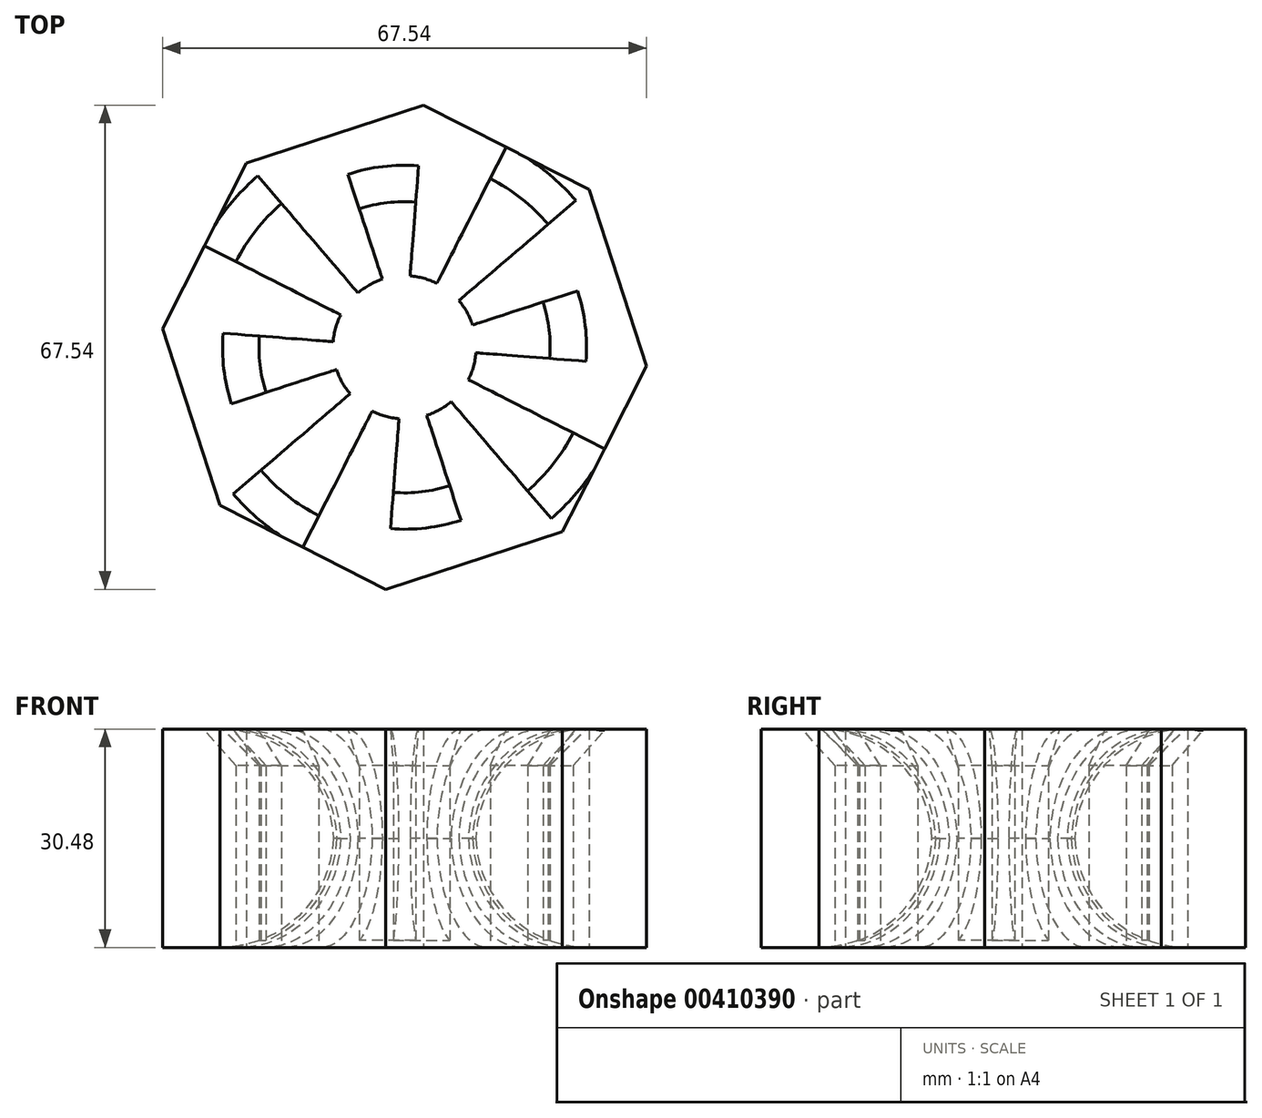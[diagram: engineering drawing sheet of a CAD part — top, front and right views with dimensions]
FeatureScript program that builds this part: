
annotation { "Feature Type Name" : "Feature", "Feature Type Description" : "" }
export const myFeature = defineFeature(function(context is Context, id is Id, definition is map)
    precondition{}
    {
        {
            var Q0;
            Q0=qCreatedBy(makeId("Top.planeOp"),FACE);
            var sketch = newSketch(context, id + "F0", { "sketchPlane" : qUnion([Q0])});
            skCircle(sketch, "E0.cCircle", {"center": v(0, 0) * mm, "radius": 31.3 * mm, "construction": true});
            skLineSegment(sketch, "E0.0", {"start": v(-33.77, 2.61) * mm, "end": v(-22.03, 25.73) * mm});
            skLineSegment(sketch, "E0.1", {"start": v(-22.03, 25.73) * mm, "end": v(2.61, 33.77) * mm});
            skLineSegment(sketch, "E0.2", {"start": v(2.61, 33.77) * mm, "end": v(25.73, 22.03) * mm});
            skLineSegment(sketch, "E0.3", {"start": v(25.73, 22.03) * mm, "end": v(33.77, -2.61) * mm});
            skLineSegment(sketch, "E0.4", {"start": v(33.77, -2.61) * mm, "end": v(22.03, -25.73) * mm});
            skLineSegment(sketch, "E0.5", {"start": v(22.03, -25.73) * mm, "end": v(-2.61, -33.77) * mm});
            skLineSegment(sketch, "E0.6", {"start": v(-2.61, -33.77) * mm, "end": v(-25.73, -22.03) * mm});
            skLineSegment(sketch, "E0.7", {"start": v(-25.73, -22.03) * mm, "end": v(-33.77, 2.61) * mm});
            skPoint(sketch, "E0.0.midPoint", {"position": v(-27.9, 14.17) * mm});
            skLineSegment(sketch, "E1", {"start": v(-0.77, -9.95) * mm, "end": v(-2.61, -33.77) * mm});
            skLineSegment(sketch, "E2", {"start": v(9.71, -29.75) * mm, "end": v(3.1, -9.49) * mm});
            skLineSegment(sketch, "E3", {"start": v(22.03, -25.73) * mm, "end": v(6.5, -7.58) * mm});
            skLineSegment(sketch, "E4", {"start": v(27.9, -14.17) * mm, "end": v(8.9, -4.52) * mm});
            skLineSegment(sketch, "E5", {"start": v(33.77, -2.61) * mm, "end": v(9.95, -0.77) * mm});
            skLineSegment(sketch, "E6", {"start": v(25.73, 22.03) * mm, "end": v(7.58, 6.5) * mm});
            skLineSegment(sketch, "E7", {"start": v(2.61, 33.77) * mm, "end": v(0.77, 9.95) * mm});
            skLineSegment(sketch, "E8", {"start": v(-22.03, 25.73) * mm, "end": v(-6.5, 7.58) * mm});
            skLineSegment(sketch, "E9", {"start": v(-33.77, 2.61) * mm, "end": v(-9.95, 0.77) * mm});
            skLineSegment(sketch, "E10", {"start": v(-25.73, -22.03) * mm, "end": v(-7.58, -6.5) * mm});
            skLineSegment(sketch, "E11", {"start": v(-14.17, -27.9) * mm, "end": v(-4.52, -8.9) * mm});
            skLineSegment(sketch, "E12", {"start": v(29.75, 9.71) * mm, "end": v(9.49, 3.1) * mm});
            skLineSegment(sketch, "E13", {"start": v(14.17, 27.9) * mm, "end": v(4.52, 8.9) * mm});
            skLineSegment(sketch, "E14", {"start": v(-9.71, 29.75) * mm, "end": v(-3.1, 9.49) * mm});
            skLineSegment(sketch, "E15", {"start": v(-27.9, 14.17) * mm, "end": v(-8.9, 4.52) * mm});
            skLineSegment(sketch, "E16", {"start": v(-29.75, -9.71) * mm, "end": v(-9.49, -3.1) * mm});
            skCircle(sketch, "E17", {"center": v(0, 0) * mm, "radius": 9.98 * mm});
            skCircle(sketch, "E18", {"center": v(0, 0) * mm, "radius": 20.32 * mm});
            skCircle(sketch, "E19", {"center": v(0, 0) * mm, "radius": 26.39 * mm});
            skSolve(sketch);
        }
        {
            var Q0;
            {var subQ1=sQuery(id+"F0.wireOp",EDGE,"E0.6");var subQ3=sQuery(id+"F0.wireOp",EDGE,"E11");var subQ4=makeQuery(id+"F0.imprint","INTERSECT",VERTEX,{"derivedFrom":[subQ1,subQ3]});Q0=makeQuery(id+"F0.imprint","IMPRINT",FACE,{"disambiguationData":[TD([[makeQuery(id+"F0.imprint","IMPRINT",EDGE,{"disambiguationData":[TD([[subQ4,-1.0]])],"derivedFrom":subQ3}),1.0]])]});}
            var Q1;
            {var subQ1=sQuery(id+"F0.wireOp",EDGE,"E0.5");var subQ3=sQuery(id+"F0.wireOp",EDGE,"E2");var subQ4=makeQuery(id+"F0.imprint","INTERSECT",VERTEX,{"derivedFrom":[subQ1,subQ3]});Q1=makeQuery(id+"F0.imprint","IMPRINT",FACE,{"disambiguationData":[TD([[makeQuery(id+"F0.imprint","IMPRINT",EDGE,{"disambiguationData":[TD([[subQ4,-1.0]])],"derivedFrom":subQ3}),1.0]])]});}
            var Q2;
            {var subQ1=sQuery(id+"F0.wireOp",EDGE,"E0.6");var subQ3=sQuery(id+"F0.wireOp",EDGE,"E11");var subQ4=makeQuery(id+"F0.imprint","INTERSECT",VERTEX,{"derivedFrom":[subQ1,subQ3]});Q2=makeQuery(id+"F0.imprint","IMPRINT",FACE,{"disambiguationData":[TD([[makeQuery(id+"F0.imprint","IMPRINT",EDGE,{"disambiguationData":[TD([[subQ4,-1.0]])],"derivedFrom":subQ3}),-1.0]])]});}
            var Q3;
            {var subQ1=sQuery(id+"F0.wireOp",EDGE,"E0.5");var subQ3=sQuery(id+"F0.wireOp",EDGE,"E2");var subQ4=makeQuery(id+"F0.imprint","INTERSECT",VERTEX,{"derivedFrom":[subQ1,subQ3]});Q3=makeQuery(id+"F0.imprint","IMPRINT",FACE,{"disambiguationData":[TD([[makeQuery(id+"F0.imprint","IMPRINT",EDGE,{"disambiguationData":[TD([[subQ4,-1.0]])],"derivedFrom":subQ3}),-1.0]])]});}
            var Q4;
            {var subQ1=sQuery(id+"F0.wireOp",EDGE,"E0.4");var subQ3=sQuery(id+"F0.wireOp",EDGE,"E4");var subQ4=makeQuery(id+"F0.imprint","INTERSECT",VERTEX,{"derivedFrom":[subQ1,subQ3]});Q4=makeQuery(id+"F0.imprint","IMPRINT",FACE,{"disambiguationData":[TD([[makeQuery(id+"F0.imprint","IMPRINT",EDGE,{"disambiguationData":[TD([[subQ4,-1.0]])],"derivedFrom":subQ3}),-1.0]])]});}
            var Q5;
            {var subQ1=sQuery(id+"F0.wireOp",EDGE,"E0.4");var subQ3=sQuery(id+"F0.wireOp",EDGE,"E4");var subQ4=makeQuery(id+"F0.imprint","INTERSECT",VERTEX,{"derivedFrom":[subQ1,subQ3]});Q5=makeQuery(id+"F0.imprint","IMPRINT",FACE,{"disambiguationData":[TD([[makeQuery(id+"F0.imprint","IMPRINT",EDGE,{"disambiguationData":[TD([[subQ4,-1.0]])],"derivedFrom":subQ3}),1.0]])]});}
            var Q6;
            {var subQ1=sQuery(id+"F0.wireOp",EDGE,"E0.3");var subQ3=sQuery(id+"F0.wireOp",EDGE,"E12");var subQ4=makeQuery(id+"F0.imprint","INTERSECT",VERTEX,{"derivedFrom":[subQ1,subQ3]});Q6=makeQuery(id+"F0.imprint","IMPRINT",FACE,{"disambiguationData":[TD([[makeQuery(id+"F0.imprint","IMPRINT",EDGE,{"disambiguationData":[TD([[subQ4,-1.0]])],"derivedFrom":subQ3}),1.0]])]});}
            var Q7;
            {var subQ1=sQuery(id+"F0.wireOp",EDGE,"E0.3");var subQ3=sQuery(id+"F0.wireOp",EDGE,"E12");var subQ4=makeQuery(id+"F0.imprint","INTERSECT",VERTEX,{"derivedFrom":[subQ1,subQ3]});Q7=makeQuery(id+"F0.imprint","IMPRINT",FACE,{"disambiguationData":[TD([[makeQuery(id+"F0.imprint","IMPRINT",EDGE,{"disambiguationData":[TD([[subQ4,-1.0]])],"derivedFrom":subQ3}),-1.0]])]});}
            var Q8;
            {var subQ1=sQuery(id+"F0.wireOp",EDGE,"E0.2");var subQ3=sQuery(id+"F0.wireOp",EDGE,"E13");var subQ4=makeQuery(id+"F0.imprint","INTERSECT",VERTEX,{"derivedFrom":[subQ1,subQ3]});Q8=makeQuery(id+"F0.imprint","IMPRINT",FACE,{"disambiguationData":[TD([[makeQuery(id+"F0.imprint","IMPRINT",EDGE,{"disambiguationData":[TD([[subQ4,-1.0]])],"derivedFrom":subQ3}),1.0]])]});}
            var Q9;
            {var subQ1=sQuery(id+"F0.wireOp",EDGE,"E0.2");var subQ3=sQuery(id+"F0.wireOp",EDGE,"E13");var subQ4=makeQuery(id+"F0.imprint","INTERSECT",VERTEX,{"derivedFrom":[subQ1,subQ3]});Q9=makeQuery(id+"F0.imprint","IMPRINT",FACE,{"disambiguationData":[TD([[makeQuery(id+"F0.imprint","IMPRINT",EDGE,{"disambiguationData":[TD([[subQ4,-1.0]])],"derivedFrom":subQ3}),-1.0]])]});}
            var Q10;
            {var subQ1=sQuery(id+"F0.wireOp",EDGE,"E0.1");var subQ3=sQuery(id+"F0.wireOp",EDGE,"E14");var subQ4=makeQuery(id+"F0.imprint","INTERSECT",VERTEX,{"derivedFrom":[subQ1,subQ3]});Q10=makeQuery(id+"F0.imprint","IMPRINT",FACE,{"disambiguationData":[TD([[makeQuery(id+"F0.imprint","IMPRINT",EDGE,{"disambiguationData":[TD([[subQ4,-1.0]])],"derivedFrom":subQ3}),1.0]])]});}
            var Q11;
            {var subQ1=sQuery(id+"F0.wireOp",EDGE,"E0.1");var subQ3=sQuery(id+"F0.wireOp",EDGE,"E14");var subQ4=makeQuery(id+"F0.imprint","INTERSECT",VERTEX,{"derivedFrom":[subQ1,subQ3]});Q11=makeQuery(id+"F0.imprint","IMPRINT",FACE,{"disambiguationData":[TD([[makeQuery(id+"F0.imprint","IMPRINT",EDGE,{"disambiguationData":[TD([[subQ4,-1.0]])],"derivedFrom":subQ3}),-1.0]])]});}
            var Q12;
            {var subQ1=sQuery(id+"F0.wireOp",EDGE,"E0.0");var subQ3=sQuery(id+"F0.wireOp",EDGE,"E15");var subQ4=makeQuery(id+"F0.imprint","INTERSECT",VERTEX,{"derivedFrom":[subQ1,subQ3]});Q12=makeQuery(id+"F0.imprint","IMPRINT",FACE,{"disambiguationData":[TD([[makeQuery(id+"F0.imprint","IMPRINT",EDGE,{"disambiguationData":[TD([[subQ4,-1.0]])],"derivedFrom":subQ3}),-1.0]])]});}
            var Q13;
            {var subQ1=sQuery(id+"F0.wireOp",EDGE,"E0.0");var subQ3=sQuery(id+"F0.wireOp",EDGE,"E15");var subQ4=makeQuery(id+"F0.imprint","INTERSECT",VERTEX,{"derivedFrom":[subQ1,subQ3]});Q13=makeQuery(id+"F0.imprint","IMPRINT",FACE,{"disambiguationData":[TD([[makeQuery(id+"F0.imprint","IMPRINT",EDGE,{"disambiguationData":[TD([[subQ4,-1.0]])],"derivedFrom":subQ3}),1.0]])]});}
            var Q14;
            {var subQ1=sQuery(id+"F0.wireOp",EDGE,"E0.7");var subQ3=sQuery(id+"F0.wireOp",EDGE,"E16");var subQ4=makeQuery(id+"F0.imprint","INTERSECT",VERTEX,{"derivedFrom":[subQ1,subQ3]});Q14=makeQuery(id+"F0.imprint","IMPRINT",FACE,{"disambiguationData":[TD([[makeQuery(id+"F0.imprint","IMPRINT",EDGE,{"disambiguationData":[TD([[subQ4,-1.0]])],"derivedFrom":subQ3}),1.0]])]});}
            var Q15;
            {var subQ1=sQuery(id+"F0.wireOp",EDGE,"E0.7");var subQ3=sQuery(id+"F0.wireOp",EDGE,"E16");var subQ4=makeQuery(id+"F0.imprint","INTERSECT",VERTEX,{"derivedFrom":[subQ1,subQ3]});Q15=makeQuery(id+"F0.imprint","IMPRINT",FACE,{"disambiguationData":[TD([[makeQuery(id+"F0.imprint","IMPRINT",EDGE,{"disambiguationData":[TD([[subQ4,-1.0]])],"derivedFrom":subQ3}),-1.0]])]});}
            var Q16;
            {var subQ0=sQuery(id+"F0.wireOp",EDGE,"E19");var subQ1=sQuery(id+"F0.wireOp",EDGE,"E10");var subQ2=makeQuery(id+"F0.imprint","INTERSECT",VERTEX,{"derivedFrom":[subQ1,subQ0]});Q16=makeQuery(id+"F0.imprint","IMPRINT",FACE,{"disambiguationData":[TD([[makeQuery(id+"F0.imprint","IMPRINT",EDGE,{"disambiguationData":[TD([[subQ2,-1.0]])],"derivedFrom":subQ1}),1.0]])]});}
            var Q17;
            {var subQ0=sQuery(id+"F0.wireOp",EDGE,"E17");var subQ1=sQuery(id+"F0.wireOp",EDGE,"E10");var subQ2=makeQuery(id+"F0.imprint","INTERSECT",VERTEX,{"derivedFrom":[subQ1,subQ0]});Q17=makeQuery(id+"F0.imprint","IMPRINT",FACE,{"disambiguationData":[TD([[makeQuery(id+"F0.imprint","IMPRINT",EDGE,{"disambiguationData":[TD([[subQ2,1.0]])],"derivedFrom":subQ1}),1.0]])]});}
            var Q18;
            {var subQ0=sQuery(id+"F0.wireOp",EDGE,"E18");var subQ1=sQuery(id+"F0.wireOp",EDGE,"E1");var subQ2=makeQuery(id+"F0.imprint","INTERSECT",VERTEX,{"derivedFrom":[subQ1,subQ0]});Q18=makeQuery(id+"F0.imprint","IMPRINT",FACE,{"disambiguationData":[TD([[makeQuery(id+"F0.imprint","IMPRINT",EDGE,{"disambiguationData":[TD([[subQ2,-1.0]])],"derivedFrom":subQ1}),-1.0]])]});}
            var Q19;
            {var subQ0=sQuery(id+"F0.wireOp",EDGE,"E17");var subQ1=sQuery(id+"F0.wireOp",EDGE,"E1");var subQ2=makeQuery(id+"F0.imprint","INTERSECT",VERTEX,{"derivedFrom":[subQ1,subQ0]});Q19=makeQuery(id+"F0.imprint","IMPRINT",FACE,{"disambiguationData":[TD([[makeQuery(id+"F0.imprint","IMPRINT",EDGE,{"disambiguationData":[TD([[subQ2,-1.0]])],"derivedFrom":subQ1}),-1.0]])]});}
            var Q20;
            {var subQ0=sQuery(id+"F0.wireOp",EDGE,"E18");var subQ1=sQuery(id+"F0.wireOp",EDGE,"E1");var subQ2=makeQuery(id+"F0.imprint","INTERSECT",VERTEX,{"derivedFrom":[subQ1,subQ0]});Q20=makeQuery(id+"F0.imprint","IMPRINT",FACE,{"disambiguationData":[TD([[makeQuery(id+"F0.imprint","IMPRINT",EDGE,{"disambiguationData":[TD([[subQ2,-1.0]])],"derivedFrom":subQ1}),1.0]])]});}
            var Q21;
            {var subQ0=sQuery(id+"F0.wireOp",EDGE,"E19");var subQ1=sQuery(id+"F0.wireOp",EDGE,"E2");var subQ2=makeQuery(id+"F0.imprint","INTERSECT",VERTEX,{"derivedFrom":[subQ1,subQ0]});Q21=makeQuery(id+"F0.imprint","IMPRINT",FACE,{"disambiguationData":[TD([[makeQuery(id+"F0.imprint","IMPRINT",EDGE,{"disambiguationData":[TD([[subQ2,-1.0]])],"derivedFrom":subQ1}),-1.0]])]});}
            var Q22;
            {var subQ0=sQuery(id+"F0.wireOp",EDGE,"E17");var subQ1=sQuery(id+"F0.wireOp",EDGE,"E2");var subQ2=makeQuery(id+"F0.imprint","INTERSECT",VERTEX,{"derivedFrom":[subQ1,subQ0]});Q22=makeQuery(id+"F0.imprint","IMPRINT",FACE,{"disambiguationData":[TD([[makeQuery(id+"F0.imprint","IMPRINT",EDGE,{"disambiguationData":[TD([[subQ2,1.0]])],"derivedFrom":subQ1}),-1.0]])]});}
            var Q23;
            {var subQ0=sQuery(id+"F0.wireOp",EDGE,"E19");var subQ1=sQuery(id+"F0.wireOp",EDGE,"E4");var subQ2=makeQuery(id+"F0.imprint","INTERSECT",VERTEX,{"derivedFrom":[subQ1,subQ0]});Q23=makeQuery(id+"F0.imprint","IMPRINT",FACE,{"disambiguationData":[TD([[makeQuery(id+"F0.imprint","IMPRINT",EDGE,{"disambiguationData":[TD([[subQ2,-1.0]])],"derivedFrom":subQ1}),-1.0]])]});}
            var Q24;
            {var subQ0=sQuery(id+"F0.wireOp",EDGE,"E17");var subQ1=sQuery(id+"F0.wireOp",EDGE,"E4");var subQ2=makeQuery(id+"F0.imprint","INTERSECT",VERTEX,{"derivedFrom":[subQ1,subQ0]});Q24=makeQuery(id+"F0.imprint","IMPRINT",FACE,{"disambiguationData":[TD([[makeQuery(id+"F0.imprint","IMPRINT",EDGE,{"disambiguationData":[TD([[subQ2,1.0]])],"derivedFrom":subQ1}),-1.0]])]});}
            var Q25;
            {var subQ0=sQuery(id+"F0.wireOp",EDGE,"E19");var subQ1=sQuery(id+"F0.wireOp",EDGE,"E5");var subQ2=makeQuery(id+"F0.imprint","INTERSECT",VERTEX,{"derivedFrom":[subQ1,subQ0]});Q25=makeQuery(id+"F0.imprint","IMPRINT",FACE,{"disambiguationData":[TD([[makeQuery(id+"F0.imprint","IMPRINT",EDGE,{"disambiguationData":[TD([[subQ2,-1.0]])],"derivedFrom":subQ1}),-1.0]])]});}
            var Q26;
            {var subQ0=sQuery(id+"F0.wireOp",EDGE,"E19");var subQ1=sQuery(id+"F0.wireOp",EDGE,"E6");var subQ2=makeQuery(id+"F0.imprint","INTERSECT",VERTEX,{"derivedFrom":[subQ1,subQ0]});Q26=makeQuery(id+"F0.imprint","IMPRINT",FACE,{"disambiguationData":[TD([[makeQuery(id+"F0.imprint","IMPRINT",EDGE,{"disambiguationData":[TD([[subQ2,-1.0]])],"derivedFrom":subQ1}),1.0]])]});}
            var Q27;
            {var subQ0=sQuery(id+"F0.wireOp",EDGE,"E17");var subQ1=sQuery(id+"F0.wireOp",EDGE,"E6");var subQ2=makeQuery(id+"F0.imprint","INTERSECT",VERTEX,{"derivedFrom":[subQ1,subQ0]});Q27=makeQuery(id+"F0.imprint","IMPRINT",FACE,{"disambiguationData":[TD([[makeQuery(id+"F0.imprint","IMPRINT",EDGE,{"disambiguationData":[TD([[subQ2,1.0]])],"derivedFrom":subQ1}),1.0]])]});}
            var Q28;
            {var subQ0=sQuery(id+"F0.wireOp",EDGE,"E19");var subQ1=sQuery(id+"F0.wireOp",EDGE,"E7");var subQ2=makeQuery(id+"F0.imprint","INTERSECT",VERTEX,{"derivedFrom":[subQ1,subQ0]});Q28=makeQuery(id+"F0.imprint","IMPRINT",FACE,{"disambiguationData":[TD([[makeQuery(id+"F0.imprint","IMPRINT",EDGE,{"disambiguationData":[TD([[subQ2,-1.0]])],"derivedFrom":subQ1}),1.0]])]});}
            var Q29;
            {var subQ0=sQuery(id+"F0.wireOp",EDGE,"E17");var subQ1=sQuery(id+"F0.wireOp",EDGE,"E7");var subQ2=makeQuery(id+"F0.imprint","INTERSECT",VERTEX,{"derivedFrom":[subQ1,subQ0]});Q29=makeQuery(id+"F0.imprint","IMPRINT",FACE,{"disambiguationData":[TD([[makeQuery(id+"F0.imprint","IMPRINT",EDGE,{"disambiguationData":[TD([[subQ2,1.0]])],"derivedFrom":subQ1}),1.0]])]});}
            var Q30;
            {var subQ0=sQuery(id+"F0.wireOp",EDGE,"E19");var subQ1=sQuery(id+"F0.wireOp",EDGE,"E7");var subQ2=makeQuery(id+"F0.imprint","INTERSECT",VERTEX,{"derivedFrom":[subQ1,subQ0]});Q30=makeQuery(id+"F0.imprint","IMPRINT",FACE,{"disambiguationData":[TD([[makeQuery(id+"F0.imprint","IMPRINT",EDGE,{"disambiguationData":[TD([[subQ2,-1.0]])],"derivedFrom":subQ1}),-1.0]])]});}
            var Q31;
            {var subQ0=sQuery(id+"F0.wireOp",EDGE,"E19");var subQ1=sQuery(id+"F0.wireOp",EDGE,"E8");var subQ2=makeQuery(id+"F0.imprint","INTERSECT",VERTEX,{"derivedFrom":[subQ1,subQ0]});Q31=makeQuery(id+"F0.imprint","IMPRINT",FACE,{"disambiguationData":[TD([[makeQuery(id+"F0.imprint","IMPRINT",EDGE,{"disambiguationData":[TD([[subQ2,-1.0]])],"derivedFrom":subQ1}),1.0]])]});}
            var Q32;
            {var subQ0=sQuery(id+"F0.wireOp",EDGE,"E17");var subQ1=sQuery(id+"F0.wireOp",EDGE,"E8");var subQ2=makeQuery(id+"F0.imprint","INTERSECT",VERTEX,{"derivedFrom":[subQ1,subQ0]});Q32=makeQuery(id+"F0.imprint","IMPRINT",FACE,{"disambiguationData":[TD([[makeQuery(id+"F0.imprint","IMPRINT",EDGE,{"disambiguationData":[TD([[subQ2,1.0]])],"derivedFrom":subQ1}),1.0]])]});}
            var Q33;
            {var subQ0=sQuery(id+"F0.wireOp",EDGE,"E17");var subQ1=sQuery(id+"F0.wireOp",EDGE,"E9");var subQ2=makeQuery(id+"F0.imprint","INTERSECT",VERTEX,{"derivedFrom":[subQ1,subQ0]});Q33=makeQuery(id+"F0.imprint","IMPRINT",FACE,{"disambiguationData":[TD([[makeQuery(id+"F0.imprint","IMPRINT",EDGE,{"disambiguationData":[TD([[subQ2,1.0]])],"derivedFrom":subQ1}),1.0]])]});}
            var Q34;
            {var subQ0=sQuery(id+"F0.wireOp",EDGE,"E19");var subQ1=sQuery(id+"F0.wireOp",EDGE,"E9");var subQ2=makeQuery(id+"F0.imprint","INTERSECT",VERTEX,{"derivedFrom":[subQ1,subQ0]});Q34=makeQuery(id+"F0.imprint","IMPRINT",FACE,{"disambiguationData":[TD([[makeQuery(id+"F0.imprint","IMPRINT",EDGE,{"disambiguationData":[TD([[subQ2,-1.0]])],"derivedFrom":subQ1}),1.0]])]});}
            var Q35;
            {var subQ0=sQuery(id+"F0.wireOp",EDGE,"E19");var subQ1=sQuery(id+"F0.wireOp",EDGE,"E9");var subQ2=makeQuery(id+"F0.imprint","INTERSECT",VERTEX,{"derivedFrom":[subQ1,subQ0]});Q35=makeQuery(id+"F0.imprint","IMPRINT",FACE,{"disambiguationData":[TD([[makeQuery(id+"F0.imprint","IMPRINT",EDGE,{"disambiguationData":[TD([[subQ2,-1.0]])],"derivedFrom":subQ1}),-1.0]])]});}
            extrude(context, id + "F1", {"entities" : qUnion([Q0, Q1, Q2, Q3, Q4, Q5, Q6, Q7, Q8, Q9, Q10, Q11, Q12, Q13, Q14, Q15, Q16, Q17, Q18, Q19, Q20, Q21, Q22, Q23, Q24, Q25, Q26, Q27, Q28, Q29, Q30, Q31, Q32, Q33, Q34, Q35]), "depth" : 30.48 * mm, "offsetDistance" : 25.4 * mm});
        }
        {
            var Q0;
            {var subQ0=sQuery(id+"F0.wireOp",EDGE,"E19");Q0=makeQuery(id+"F1.opExtrude","CAP_EDGE",EDGE,{"disambiguationData":[OSD([subQ0]),TDD([makeQuery(id+"F0.imprint","IMPRINT",EDGE,{"disambiguationData":[TD([[makeQuery(id+"F0.imprint","INTERSECT",VERTEX,{"derivedFrom":[sQuery(id+"F0.wireOp",EDGE,"E3"),subQ0]}),-1.0]])],"derivedFrom":subQ0})])],"isStart":false});}
            var Q1;
            {var subQ0=sQuery(id+"F0.wireOp",EDGE,"E18");Q1=makeQuery(id+"F1.opExtrude","CAP_EDGE",EDGE,{"disambiguationData":[OSD([subQ0]),TDD([makeQuery(id+"F0.imprint","IMPRINT",EDGE,{"disambiguationData":[TD([[makeQuery(id+"F0.imprint","INTERSECT",VERTEX,{"derivedFrom":[sQuery(id+"F0.wireOp",EDGE,"E1"),subQ0]}),-1.0]])],"derivedFrom":subQ0})])],"isStart":false});}
            var Q2;
            {var subQ0=sQuery(id+"F0.wireOp",EDGE,"E19");Q2=makeQuery(id+"F1.opExtrude","CAP_EDGE",EDGE,{"disambiguationData":[OSD([subQ0]),TDD([makeQuery(id+"F0.imprint","IMPRINT",EDGE,{"disambiguationData":[TD([[makeQuery(id+"F0.imprint","INTERSECT",VERTEX,{"derivedFrom":[sQuery(id+"F0.wireOp",EDGE,"E10"),subQ0]}),-1.0]])],"derivedFrom":subQ0})])],"isStart":false});}
            var Q3;
            {var subQ0=sQuery(id+"F0.wireOp",EDGE,"E18");Q3=makeQuery(id+"F1.opExtrude","CAP_EDGE",EDGE,{"disambiguationData":[OSD([subQ0]),TDD([makeQuery(id+"F0.imprint","IMPRINT",EDGE,{"disambiguationData":[TD([[makeQuery(id+"F0.imprint","INTERSECT",VERTEX,{"derivedFrom":[sQuery(id+"F0.wireOp",EDGE,"E5"),subQ0]}),-1.0]])],"derivedFrom":subQ0})])],"isStart":false});}
            var Q4;
            {var subQ0=sQuery(id+"F0.wireOp",EDGE,"E19");Q4=makeQuery(id+"F1.opExtrude","CAP_EDGE",EDGE,{"disambiguationData":[OSD([subQ0]),TDD([makeQuery(id+"F0.imprint","IMPRINT",EDGE,{"disambiguationData":[TD([[makeQuery(id+"F0.imprint","INTERSECT",VERTEX,{"derivedFrom":[sQuery(id+"F0.wireOp",EDGE,"E6"),subQ0]}),-1.0]])],"derivedFrom":subQ0})])],"isStart":false});}
            var Q5;
            {var subQ0=sQuery(id+"F0.wireOp",EDGE,"E18");Q5=makeQuery(id+"F1.opExtrude","CAP_EDGE",EDGE,{"disambiguationData":[OSD([subQ0]),TDD([makeQuery(id+"F0.imprint","IMPRINT",EDGE,{"disambiguationData":[TD([[makeQuery(id+"F0.imprint","INTERSECT",VERTEX,{"derivedFrom":[sQuery(id+"F0.wireOp",EDGE,"E7"),subQ0]}),-1.0]])],"derivedFrom":subQ0})])],"isStart":false});}
            var Q6;
            {var subQ0=sQuery(id+"F0.wireOp",EDGE,"E19");Q6=makeQuery(id+"F1.opExtrude","CAP_EDGE",EDGE,{"disambiguationData":[OSD([subQ0]),TDD([makeQuery(id+"F0.imprint","IMPRINT",EDGE,{"disambiguationData":[TD([[makeQuery(id+"F0.imprint","INTERSECT",VERTEX,{"derivedFrom":[sQuery(id+"F0.wireOp",EDGE,"E8"),subQ0]}),-1.0]])],"derivedFrom":subQ0})])],"isStart":false});}
            var Q7;
            {var subQ0=sQuery(id+"F0.wireOp",EDGE,"E18");Q7=makeQuery(id+"F1.opExtrude","CAP_EDGE",EDGE,{"disambiguationData":[OSD([subQ0]),TDD([makeQuery(id+"F0.imprint","IMPRINT",EDGE,{"disambiguationData":[TD([[makeQuery(id+"F0.imprint","INTERSECT",VERTEX,{"derivedFrom":[sQuery(id+"F0.wireOp",EDGE,"E9"),subQ0]}),-1.0]])],"derivedFrom":subQ0})])],"isStart":false});}
            chamfer(context, id + "F2", {"entities" : qUnion([Q0, Q1, Q2, Q3, Q4, Q5, Q6, Q7]), "width" : 5.08 * mm, "tangentPropagation" : true});
        }
        {
            var Q0;
            {var subQ0=sQuery(id+"F0.wireOp",EDGE,"E17");Q0=makeQuery(id+"F1.opExtrude","CAP_EDGE",EDGE,{"disambiguationData":[OSD([subQ0]),TDD([makeQuery(id+"F0.imprint","IMPRINT",EDGE,{"disambiguationData":[TD([[makeQuery(id+"F0.imprint","INTERSECT",VERTEX,{"derivedFrom":[sQuery(id+"F0.wireOp",EDGE,"E9"),subQ0]}),1.0]])],"derivedFrom":subQ0})])],"isStart":false});}
            var Q1;
            {var subQ0=sQuery(id+"F0.wireOp",EDGE,"E17");Q1=makeQuery(id+"F1.opExtrude","CAP_EDGE",EDGE,{"disambiguationData":[OSD([subQ0]),TDD([makeQuery(id+"F0.imprint","IMPRINT",EDGE,{"disambiguationData":[TD([[makeQuery(id+"F0.imprint","INTERSECT",VERTEX,{"derivedFrom":[sQuery(id+"F0.wireOp",EDGE,"E8"),subQ0]}),1.0]])],"derivedFrom":subQ0})])],"isStart":false});}
            var Q2;
            {var subQ0=sQuery(id+"F0.wireOp",EDGE,"E17");Q2=makeQuery(id+"F1.opExtrude","CAP_EDGE",EDGE,{"disambiguationData":[OSD([subQ0]),TDD([makeQuery(id+"F0.imprint","IMPRINT",EDGE,{"disambiguationData":[TD([[makeQuery(id+"F0.imprint","INTERSECT",VERTEX,{"derivedFrom":[sQuery(id+"F0.wireOp",EDGE,"E7"),subQ0]}),1.0]])],"derivedFrom":subQ0})])],"isStart":false});}
            var Q3;
            {var subQ0=sQuery(id+"F0.wireOp",EDGE,"E17");Q3=makeQuery(id+"F1.opExtrude","CAP_EDGE",EDGE,{"disambiguationData":[OSD([subQ0]),TDD([makeQuery(id+"F0.imprint","IMPRINT",EDGE,{"disambiguationData":[TD([[makeQuery(id+"F0.imprint","INTERSECT",VERTEX,{"derivedFrom":[sQuery(id+"F0.wireOp",EDGE,"E6"),subQ0]}),1.0]])],"derivedFrom":subQ0})])],"isStart":false});}
            var Q4;
            {var subQ0=sQuery(id+"F0.wireOp",EDGE,"E17");Q4=makeQuery(id+"F1.opExtrude","CAP_EDGE",EDGE,{"disambiguationData":[OSD([subQ0]),TDD([makeQuery(id+"F0.imprint","IMPRINT",EDGE,{"disambiguationData":[TD([[makeQuery(id+"F0.imprint","INTERSECT",VERTEX,{"derivedFrom":[sQuery(id+"F0.wireOp",EDGE,"E4"),subQ0]}),-1.0]])],"derivedFrom":subQ0})])],"isStart":false});}
            var Q5;
            {var subQ0=sQuery(id+"F0.wireOp",EDGE,"E17");Q5=makeQuery(id+"F1.opExtrude","CAP_EDGE",EDGE,{"disambiguationData":[OSD([subQ0]),TDD([makeQuery(id+"F0.imprint","IMPRINT",EDGE,{"disambiguationData":[TD([[makeQuery(id+"F0.imprint","INTERSECT",VERTEX,{"derivedFrom":[sQuery(id+"F0.wireOp",EDGE,"E2"),subQ0]}),-1.0]])],"derivedFrom":subQ0})])],"isStart":false});}
            var Q6;
            {var subQ0=sQuery(id+"F0.wireOp",EDGE,"E17");Q6=makeQuery(id+"F1.opExtrude","CAP_EDGE",EDGE,{"disambiguationData":[OSD([subQ0]),TDD([makeQuery(id+"F0.imprint","IMPRINT",EDGE,{"disambiguationData":[TD([[makeQuery(id+"F0.imprint","INTERSECT",VERTEX,{"derivedFrom":[sQuery(id+"F0.wireOp",EDGE,"E1"),subQ0]}),1.0]])],"derivedFrom":subQ0})])],"isStart":false});}
            var Q7;
            {var subQ0=sQuery(id+"F0.wireOp",EDGE,"E17");Q7=makeQuery(id+"F1.opExtrude","CAP_EDGE",EDGE,{"disambiguationData":[OSD([subQ0]),TDD([makeQuery(id+"F0.imprint","IMPRINT",EDGE,{"disambiguationData":[TD([[makeQuery(id+"F0.imprint","INTERSECT",VERTEX,{"derivedFrom":[sQuery(id+"F0.wireOp",EDGE,"E10"),subQ0]}),1.0]])],"derivedFrom":subQ0})])],"isStart":false});}
            var Q8;
            {var subQ0=sQuery(id+"F0.wireOp",EDGE,"E17");Q8=makeQuery(id+"F1.opExtrude","CAP_EDGE",EDGE,{"disambiguationData":[OSD([subQ0]),TDD([makeQuery(id+"F0.imprint","IMPRINT",EDGE,{"disambiguationData":[TD([[makeQuery(id+"F0.imprint","INTERSECT",VERTEX,{"derivedFrom":[sQuery(id+"F0.wireOp",EDGE,"E7"),subQ0]}),1.0]])],"derivedFrom":subQ0})])],"isStart":true});}
            var Q9;
            {var subQ0=sQuery(id+"F0.wireOp",EDGE,"E17");Q9=makeQuery(id+"F1.opExtrude","CAP_EDGE",EDGE,{"disambiguationData":[OSD([subQ0]),TDD([makeQuery(id+"F0.imprint","IMPRINT",EDGE,{"disambiguationData":[TD([[makeQuery(id+"F0.imprint","INTERSECT",VERTEX,{"derivedFrom":[sQuery(id+"F0.wireOp",EDGE,"E6"),subQ0]}),1.0]])],"derivedFrom":subQ0})])],"isStart":true});}
            var Q10;
            {var subQ0=sQuery(id+"F0.wireOp",EDGE,"E17");Q10=makeQuery(id+"F1.opExtrude","CAP_EDGE",EDGE,{"disambiguationData":[OSD([subQ0]),TDD([makeQuery(id+"F0.imprint","IMPRINT",EDGE,{"disambiguationData":[TD([[makeQuery(id+"F0.imprint","INTERSECT",VERTEX,{"derivedFrom":[sQuery(id+"F0.wireOp",EDGE,"E4"),subQ0]}),-1.0]])],"derivedFrom":subQ0})])],"isStart":true});}
            var Q11;
            {var subQ0=sQuery(id+"F0.wireOp",EDGE,"E17");Q11=makeQuery(id+"F1.opExtrude","CAP_EDGE",EDGE,{"disambiguationData":[OSD([subQ0]),TDD([makeQuery(id+"F0.imprint","IMPRINT",EDGE,{"disambiguationData":[TD([[makeQuery(id+"F0.imprint","INTERSECT",VERTEX,{"derivedFrom":[sQuery(id+"F0.wireOp",EDGE,"E2"),subQ0]}),-1.0]])],"derivedFrom":subQ0})])],"isStart":true});}
            var Q12;
            {var subQ0=sQuery(id+"F0.wireOp",EDGE,"E17");Q12=makeQuery(id+"F1.opExtrude","CAP_EDGE",EDGE,{"disambiguationData":[OSD([subQ0]),TDD([makeQuery(id+"F0.imprint","IMPRINT",EDGE,{"disambiguationData":[TD([[makeQuery(id+"F0.imprint","INTERSECT",VERTEX,{"derivedFrom":[sQuery(id+"F0.wireOp",EDGE,"E1"),subQ0]}),1.0]])],"derivedFrom":subQ0})])],"isStart":true});}
            var Q13;
            {var subQ0=sQuery(id+"F0.wireOp",EDGE,"E17");Q13=makeQuery(id+"F1.opExtrude","CAP_EDGE",EDGE,{"disambiguationData":[OSD([subQ0]),TDD([makeQuery(id+"F0.imprint","IMPRINT",EDGE,{"disambiguationData":[TD([[makeQuery(id+"F0.imprint","INTERSECT",VERTEX,{"derivedFrom":[sQuery(id+"F0.wireOp",EDGE,"E10"),subQ0]}),1.0]])],"derivedFrom":subQ0})])],"isStart":true});}
            var Q14;
            {var subQ0=sQuery(id+"F0.wireOp",EDGE,"E17");Q14=makeQuery(id+"F1.opExtrude","CAP_EDGE",EDGE,{"disambiguationData":[OSD([subQ0]),TDD([makeQuery(id+"F0.imprint","IMPRINT",EDGE,{"disambiguationData":[TD([[makeQuery(id+"F0.imprint","INTERSECT",VERTEX,{"derivedFrom":[sQuery(id+"F0.wireOp",EDGE,"E9"),subQ0]}),1.0]])],"derivedFrom":subQ0})])],"isStart":true});}
            var Q15;
            {var subQ0=sQuery(id+"F0.wireOp",EDGE,"E17");Q15=makeQuery(id+"F1.opExtrude","CAP_EDGE",EDGE,{"disambiguationData":[OSD([subQ0]),TDD([makeQuery(id+"F0.imprint","IMPRINT",EDGE,{"disambiguationData":[TD([[makeQuery(id+"F0.imprint","INTERSECT",VERTEX,{"derivedFrom":[sQuery(id+"F0.wireOp",EDGE,"E8"),subQ0]}),1.0]])],"derivedFrom":subQ0})])],"isStart":true});}
            fillet(context, id + "F3", {"entities" : qUnion([Q0, Q1, Q2, Q3, Q4, Q5, Q6, Q7, Q8, Q9, Q10, Q11, Q12, Q13, Q14, Q15]), "radius" : 15.76 * mm, "tangentPropagation" : true, "allowEdgeOverflow" : false});
        }
    });
